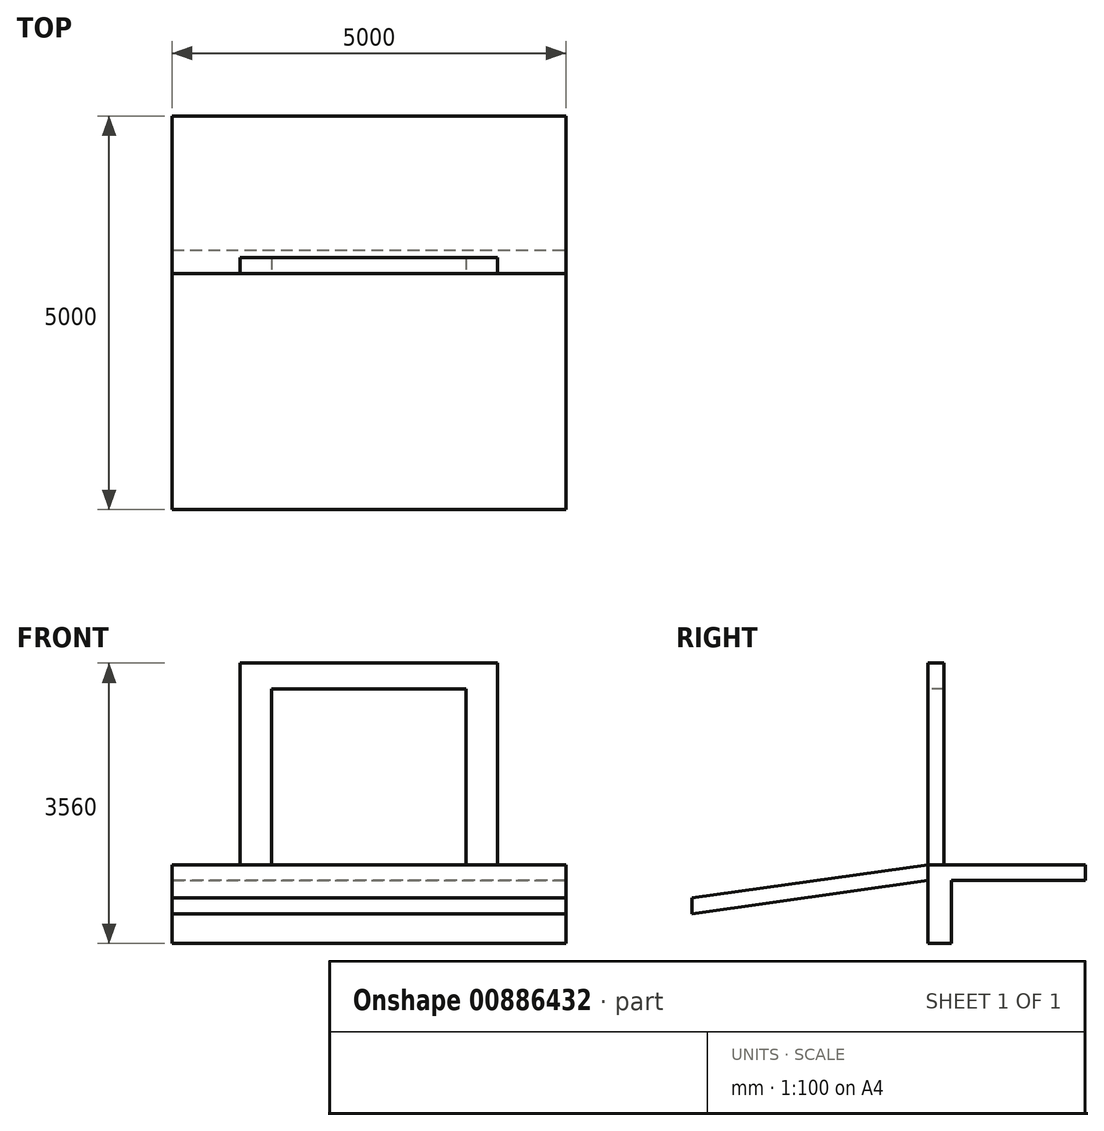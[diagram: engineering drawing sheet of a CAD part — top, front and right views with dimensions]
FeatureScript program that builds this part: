
annotation { "Feature Type Name" : "Feature", "Feature Type Description" : "" }
export const myFeature = defineFeature(function(context is Context, id is Id, definition is map)
    precondition{}
    {
        {
            var Q0;
            Q0=qCreatedBy(makeId("Front.planeOp"),FACE);
            var sketch = newSketch(context, id + "F0", { "sketchPlane" : qUnion([Q0])});
            skLineSegment(sketch, "E0.bottom", {"start": v(1235, 2230) * mm, "end": v(-1235, 2230) * mm});
            skLineSegment(sketch, "E0.top", {"start": v(1235, 0) * mm, "end": v(-1235, 0) * mm});
            skLineSegment(sketch, "E0.left", {"start": v(1235, 2230) * mm, "end": v(1235, 0) * mm});
            skLineSegment(sketch, "E0.right", {"start": v(-1235, 2230) * mm, "end": v(-1235, 0) * mm});
            skPoint(sketch, "E0.middle", {"position": v(0, 1115) * mm});
            skLineSegment(sketch, "E1", {"start": v(1235, 0) * mm, "end": v(1635, 0) * mm});
            skLineSegment(sketch, "E2", {"start": v(1635, 0) * mm, "end": v(1635, 2560) * mm});
            skLineSegment(sketch, "E3", {"start": v(1635, 2560) * mm, "end": v(-1635, 2560) * mm});
            skLineSegment(sketch, "E4", {"start": v(0, 0) * mm, "end": v(0, 1445.82) * mm, "construction": true});
            skLineSegment(sketch, "E5.MirrorCS", {"start": v(-1635, 0) * mm, "end": v(-1635, 2560) * mm});
            skLineSegment(sketch, "E6", {"start": v(-1235, 0) * mm, "end": v(-1635, 0) * mm});
            skSolve(sketch);
        }
        {
            var Q0;
            Q0=makeQuery(id+"F0.imprint","IMPRINT",FACE,{"disambiguationData":[TD([[makeQuery(id+"F0.imprint","IMPRINT",EDGE,{"derivedFrom":sQuery(id+"F0.wireOp",EDGE,"E0.bottom")}),-1.0]])]});
            extrude(context, id + "F1", {"entities" : qUnion([Q0]), "oppositeDirection" : true, "depth" : 200 * mm, "offsetDistance" : 25 * mm});
        }
        {
            var Q0;
            Q0=qCreatedBy(makeId("Right.planeOp"),FACE);
            var sketch = newSketch(context, id + "F2", { "sketchPlane" : qUnion([Q0])});
            skLineSegment(sketch, "E7", {"start": v(0, 0) * mm, "end": v(-3000, 0) * mm, "construction": true});
            skLineSegment(sketch, "E8", {"start": v(0, 0) * mm, "end": v(-3000, -421.62) * mm});
            skLineSegment(sketch, "E9", {"start": v(-3000, -421.62) * mm, "end": v(-3000, 0) * mm, "construction": true});
            skLineSegment(sketch, "E10", {"start": v(0, 0) * mm, "end": v(0, -201.97) * mm});
            skLineSegment(sketch, "E11.0", {"start": v(0, -201.97) * mm, "end": v(-3000, -623.59) * mm});
            skLineSegment(sketch, "E12", {"start": v(-3000, -421.62) * mm, "end": v(-3000, -623.59) * mm});
            skSolve(sketch);
        }
        {
            var Q0;
            Q0 = qSketchRegion(id + "F2", true);
            extrude(context, id + "F3", {"entities" : qUnion([Q0]), "endBound" : BoundingType.SYMMETRIC, "depth" : 5000 * mm, "offsetDistance" : 25 * mm});
        }
        {
            var Q0;
            Q0=qCreatedBy(makeId("Right.planeOp"),FACE);
            var sketch = newSketch(context, id + "F4", { "sketchPlane" : qUnion([Q0])});
            skLineSegment(sketch, "E13", {"start": v(0, 0) * mm, "end": v(0, -1000) * mm});
            skLineSegment(sketch, "E14", {"start": v(0, -1000) * mm, "end": v(300, -1000) * mm});
            skLineSegment(sketch, "E15", {"start": v(300, -1000) * mm, "end": v(300, -200) * mm});
            skLineSegment(sketch, "E16", {"start": v(300, -200) * mm, "end": v(2000, -200) * mm});
            skLineSegment(sketch, "E17", {"start": v(2000, -200) * mm, "end": v(2000, 0) * mm});
            skLineSegment(sketch, "E18", {"start": v(2000, 0) * mm, "end": v(0, 0) * mm});
            skSolve(sketch);
        }
        {
            var Q0;
            Q0 = qSketchRegion(id + "F4", true);
            var Q1;
            Q1=makeQuery(id+"F3.opExtrude","CAP_VERTEX",VERTEX,{"disambiguationData":[OSD([sQuery(id+"F2.wireOp",EDGE,"E8"),sQuery(id+"F2.wireOp",EDGE,"E10")])],"isStart":true});
            var Q2;
            Q2=makeQuery(id+"F3.opExtrude","CAP_VERTEX",VERTEX,{"disambiguationData":[OSD([sQuery(id+"F2.wireOp",EDGE,"E8"),sQuery(id+"F2.wireOp",EDGE,"E10")])],"isStart":false});
            extrude(context, id + "F5", {"entities" : qUnion([Q0]), "endBound" : BoundingType.UP_TO_VERTEX, "oppositeDirection" : true, "depth" : 25 * mm, "endBoundEntityVertex" : qUnion([Q1]), "offsetDistance" : 25 * mm, "hasSecondDirection" : true, "secondDirectionBound" : SecondDirectionBoundingType.UP_TO_VERTEX, "secondDirectionOppositeDirection" : false, "secondDirectionDepth" : 25 * mm, "secondDirectionBoundEntityVertex" : qUnion([Q2])});
        }
    });
